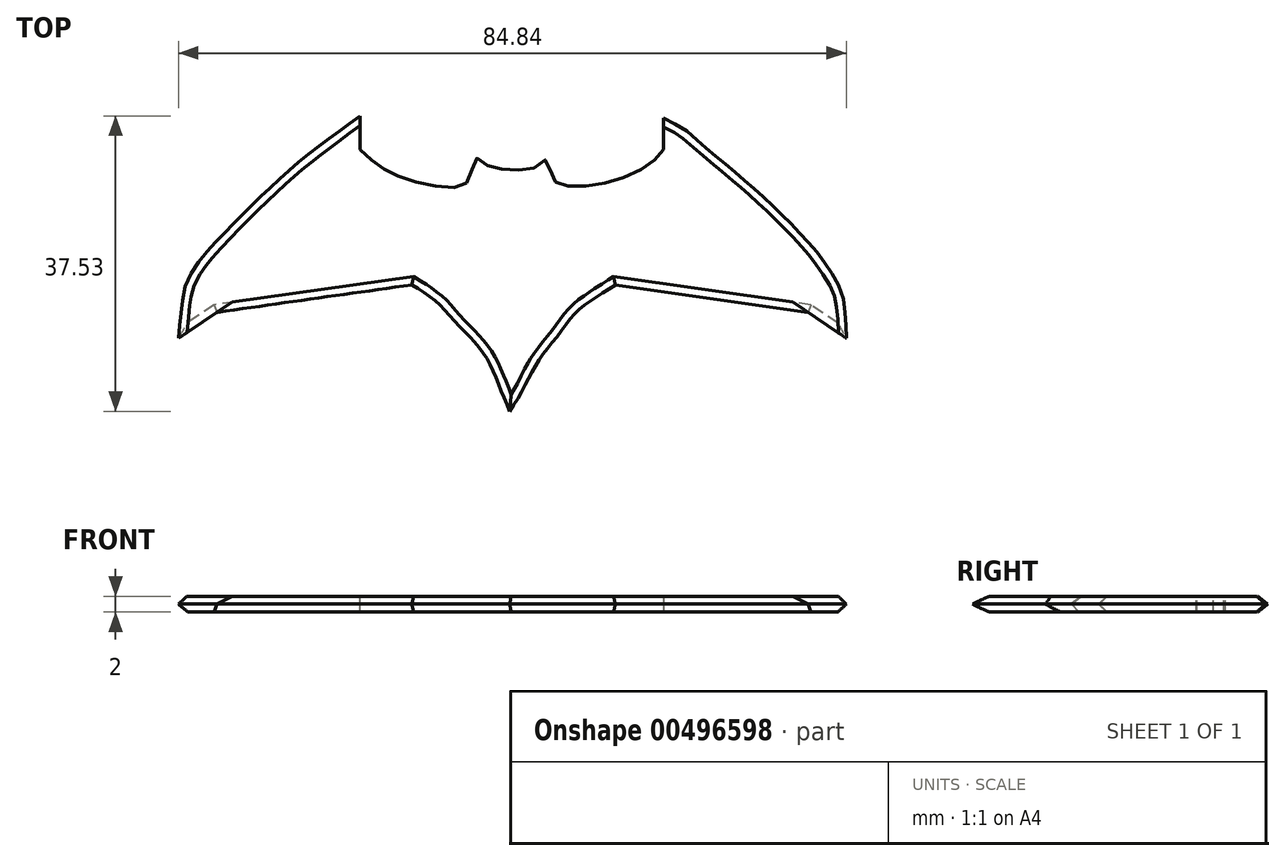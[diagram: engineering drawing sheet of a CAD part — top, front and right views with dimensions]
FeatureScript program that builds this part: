
annotation { "Feature Type Name" : "Feature", "Feature Type Description" : "" }
export const myFeature = defineFeature(function(context is Context, id is Id, definition is map)
    precondition{}
    {
        {
            var Q0;
            Q0=qCreatedBy(makeId("Top.planeOp"),FACE);
            var sketch = newSketch(context, id + "F0", { "sketchPlane" : qUnion([Q0])});
            skLineSegment(sketch, "E0", {"start": v(-19.01, 17.28) * mm, "end": v(-19.01, 12.99) * mm});
            skFitSpline(sketch, "E1", {"points": [v(-19.01, 12.99) * mm, v(-16.82, 11.1) * mm, v(-14.32, 9.7) * mm, v(-10.13, 8.5) * mm, v(-6.34, 8.3) * mm, v(-5.04, 9.5) * mm, v(-4.24, 11.89) * mm, v(-2.74, 10.9) * mm, v(0, 10.5) * mm, v(3.15, 10.7) * mm, v(4.64, 11.69) * mm, v(5.34, 9.6) * mm, v(6.64, 8.5) * mm, v(10.03, 8.4) * mm, v(14.43, 9.4) * mm, v(17.92, 11.29) * mm, v(19.52, 12.99) * mm], "startDerivative": vector(33.98, -31.52) * mm, "endDerivative": vector(24.09, 30.13) * mm});
            skLineSegment(sketch, "E2", {"start": v(19.52, 12.99) * mm, "end": v(19.52, 16.98) * mm});
            skFitSpline(sketch, "E3", {"points": [v(19.52, 16.98) * mm, v(22.01, 15.68) * mm, v(24.5, 13.59) * mm, v(27.7, 10.9) * mm, v(32, 7.2) * mm, v(36.08, 3.2) * mm, v(38.98, 0) * mm, v(41.07, -2.98) * mm, v(42.27, -5.48) * mm, v(42.77, -10.97) * mm], "startDerivative": vector(27.86, -12.46) * mm, "endDerivative": vector(1.48, -47.62) * mm});
            skLineSegment(sketch, "E4", {"start": v(42.77, -10.97) * mm, "end": v(37.88, -7.67) * mm});
            skLineSegment(sketch, "E5", {"start": v(37.88, -7.67) * mm, "end": v(13.43, -4.18) * mm});
            skFitSpline(sketch, "E6", {"points": [v(13.43, -4.18) * mm, v(10.93, -5.78) * mm, v(8.44, -7.67) * mm, v(6.24, -10.47) * mm, v(3.45, -14.16) * mm, v(1.65, -17.56) * mm, v(0, -20.25) * mm], "startDerivative": vector(-16.22, -10.3) * mm, "endDerivative": vector(-10.8, -16.48) * mm});
            skFitSpline(sketch, "E7", {"points": [v(0, -20.25) * mm, v(-1.15, -17.46) * mm, v(-3.34, -12.86) * mm, v(-6.83, -8.97) * mm, v(-9.13, -6.48) * mm, v(-12.42, -4.18) * mm], "startDerivative": vector(-6.35, 15.1) * mm, "endDerivative": vector(-18.03, 11.17) * mm});
            skLineSegment(sketch, "E8", {"start": v(-12.42, -4.18) * mm, "end": v(-37.18, -7.67) * mm});
            skLineSegment(sketch, "E9", {"start": v(-37.18, -7.67) * mm, "end": v(-42.07, -10.97) * mm});
            skPoint(sketch, "E10.3.internal.snap0", {"position": v(-39.62, -9.32) * mm});
            skFitSpline(sketch, "E10", {"points": [v(-42.07, -10.97) * mm, v(-41.43, -5.26) * mm, v(-40.91, -3.68) * mm, v(-39.62, -1.47) * mm, v(-37.95, 0.54) * mm, v(-35.19, 3.5) * mm, v(-29.14, 9.33) * mm, v(-24.44, 13.28) * mm, v(-20.86, 15.9) * mm, v(-19.01, 17.28) * mm], "startDerivative": vector(4.5, 49.97) * mm, "endDerivative": vector(19.98, 15.05) * mm});
            skSolve(sketch);
        }
        {
            var Q0;
            Q0=makeQuery(id+"F0.imprint","IMPRINT",FACE,{"disambiguationData":[TD([[makeQuery(id+"F0.imprint","IMPRINT",EDGE,{"derivedFrom":sQuery(id+"F0.wireOp",EDGE,"E0")}),-1.0]])]});
            extrude(context, id + "F1", {"entities" : qUnion([Q0]), "depth" : 2 * mm, "offsetDistance" : 25 * mm});
        }
        {
            var Q0;
            Q0=makeQuery(id+"F1.opExtrude","CAP_EDGE",EDGE,{"disambiguationData":[OSD([sQuery(id+"F0.wireOp",EDGE,"E10")])],"isStart":false});
            var Q1;
            Q1=makeQuery(id+"F1.opExtrude","CAP_EDGE",EDGE,{"disambiguationData":[OSD([sQuery(id+"F0.wireOp",EDGE,"E3")])],"isStart":false});
            var Q2;
            Q2=makeQuery(id+"F1.opExtrude","CAP_EDGE",EDGE,{"disambiguationData":[OSD([sQuery(id+"F0.wireOp",EDGE,"E6")])],"isStart":false});
            var Q3;
            Q3=makeQuery(id+"F1.opExtrude","CAP_EDGE",EDGE,{"disambiguationData":[OSD([sQuery(id+"F0.wireOp",EDGE,"E7")])],"isStart":false});
            var Q4;
            Q4=makeQuery(id+"F1.opExtrude","CAP_EDGE",EDGE,{"disambiguationData":[OSD([sQuery(id+"F0.wireOp",EDGE,"E8")])],"isStart":false});
            var Q5;
            Q5=makeQuery(id+"F1.opExtrude","CAP_EDGE",EDGE,{"disambiguationData":[OSD([sQuery(id+"F0.wireOp",EDGE,"E5")])],"isStart":false});
            var Q6;
            Q6=makeQuery(id+"F1.opExtrude","CAP_EDGE",EDGE,{"disambiguationData":[OSD([sQuery(id+"F0.wireOp",EDGE,"E3")])],"isStart":true});
            var Q7;
            Q7=makeQuery(id+"F1.opExtrude","CAP_EDGE",EDGE,{"disambiguationData":[OSD([sQuery(id+"F0.wireOp",EDGE,"E4")])],"isStart":true});
            var Q8;
            Q8=makeQuery(id+"F1.opExtrude","CAP_EDGE",EDGE,{"disambiguationData":[OSD([sQuery(id+"F0.wireOp",EDGE,"E5")])],"isStart":true});
            var Q9;
            Q9=makeQuery(id+"F1.opExtrude","CAP_EDGE",EDGE,{"disambiguationData":[OSD([sQuery(id+"F0.wireOp",EDGE,"E6")])],"isStart":true});
            var Q10;
            Q10=makeQuery(id+"F1.opExtrude","CAP_EDGE",EDGE,{"disambiguationData":[OSD([sQuery(id+"F0.wireOp",EDGE,"E7")])],"isStart":true});
            var Q11;
            Q11=makeQuery(id+"F1.opExtrude","CAP_EDGE",EDGE,{"disambiguationData":[OSD([sQuery(id+"F0.wireOp",EDGE,"E8")])],"isStart":true});
            var Q12;
            Q12=makeQuery(id+"F1.opExtrude","CAP_EDGE",EDGE,{"disambiguationData":[OSD([sQuery(id+"F0.wireOp",EDGE,"E9")])],"isStart":true});
            var Q13;
            Q13=makeQuery(id+"F1.opExtrude","CAP_EDGE",EDGE,{"disambiguationData":[OSD([sQuery(id+"F0.wireOp",EDGE,"E10")])],"isStart":true});
            chamfer(context, id + "F2", {"entities" : qUnion([Q0, Q1, Q2, Q3, Q4, Q5, Q6, Q7, Q8, Q9, Q10, Q11, Q12, Q13]), "width" : 1 * mm, "tangentPropagation" : true});
        }
    });
